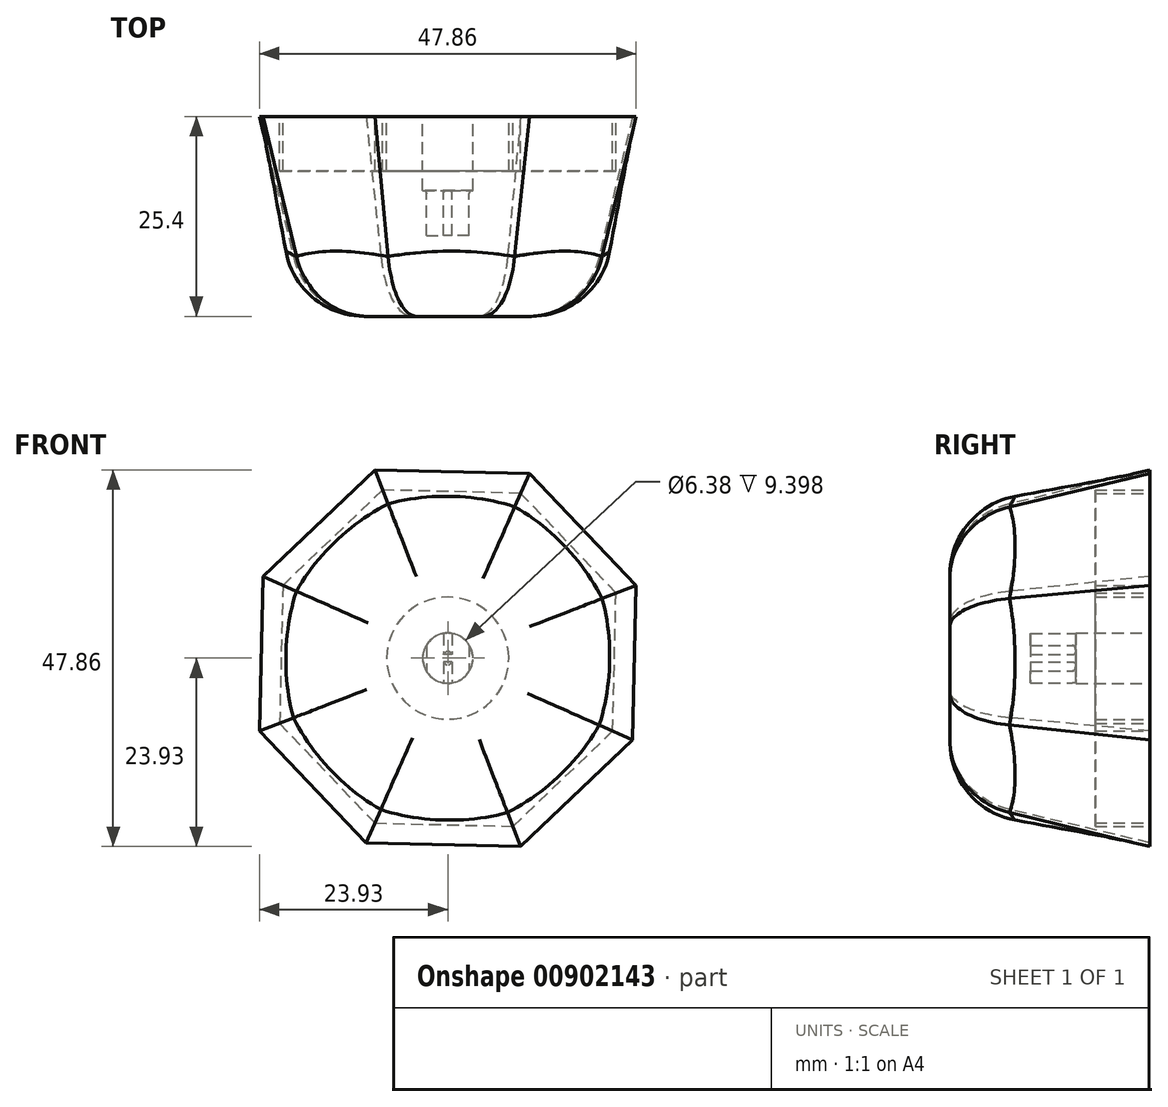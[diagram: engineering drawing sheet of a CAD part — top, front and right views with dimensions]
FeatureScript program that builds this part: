
annotation { "Feature Type Name" : "Feature", "Feature Type Description" : "" }
export const myFeature = defineFeature(function(context is Context, id is Id, definition is map)
    precondition{}
    {
        {
            var Q0;
            Q0=qCreatedBy(makeId("Front.planeOp"),FACE);
            var sketch = newSketch(context, id + "F0", { "sketchPlane" : qUnion([Q0])});
            skLineSegment(sketch, "E0.0", {"start": v(23.46, -10.38) * mm, "end": v(9.25, -23.93) * mm});
            skLineSegment(sketch, "E0.1", {"start": v(9.25, -23.93) * mm, "end": v(-10.38, -23.46) * mm});
            skLineSegment(sketch, "E0.2", {"start": v(-10.38, -23.46) * mm, "end": v(-23.93, -9.25) * mm});
            skLineSegment(sketch, "E0.3", {"start": v(-23.93, -9.25) * mm, "end": v(-23.46, 10.38) * mm});
            skLineSegment(sketch, "E0.4", {"start": v(-23.46, 10.38) * mm, "end": v(-9.25, 23.93) * mm});
            skLineSegment(sketch, "E0.5", {"start": v(-9.25, 23.93) * mm, "end": v(10.38, 23.46) * mm});
            skLineSegment(sketch, "E0.6", {"start": v(10.38, 23.46) * mm, "end": v(23.93, 9.25) * mm});
            skLineSegment(sketch, "E0.7", {"start": v(23.93, 9.25) * mm, "end": v(23.46, -10.38) * mm});
            skPoint(sketch, "E0.0.midPoint", {"position": v(16.36, -17.15) * mm});
            skSolve(sketch);
        }
        {
            var Q0;
            Q0=qCreatedBy(makeId("Front.planeOp"),FACE);
            cPlane(context, id + "F1", {"entities" : qUnion([Q0]), "cplaneType" : CPlaneType.OFFSET, "offset" : 25.4 * mm, "width" : 152.4 * mm, "height" : 152.4 * mm});
        }
        {
            var Q0;
            Q0=qCreatedBy(id+"F1.planeOp",FACE);
            var sketch = newSketch(context, id + "F2", { "sketchPlane" : qUnion([Q0])});
            skCircle(sketch, "E1", {"center": v(0, 0) * mm, "radius": 19.05 * mm});
            skSolve(sketch);
        }
        {
            var Q0;
            Q0=makeQuery(id+"F0.imprint","IMPRINT",FACE,{"disambiguationData":[TD([[makeQuery(id+"F0.imprint","IMPRINT",EDGE,{"derivedFrom":sQuery(id+"F0.wireOp",EDGE,"E0.0")}),-1.0]])]});
            var Q1;
            Q1=makeQuery(id+"F2.imprint","IMPRINT",FACE,{"disambiguationData":[TD([[makeQuery(id+"F2.imprint","IMPRINT",EDGE,{"derivedFrom":sQuery(id+"F2.wireOp",EDGE,"E1")}),1.0]])]});
            loft(context, id + "F3", {"sheetProfilesArray" : [{ "sheetProfileEntities" : qUnion([Q0]) }, { "sheetProfileEntities" : qUnion([Q1]) }]});
        }
        {
            var Q0;
            Q0=qCreatedBy(makeId("Front.planeOp"),FACE);
            var sketch = newSketch(context, id + "F4", { "sketchPlane" : qUnion([Q0])});
            skArc(sketch, "E2", {"start": v(2.72, 1.64) * mm, "mid": v(1.8, 2.62) * mm, "end": v(0.56, 3.13) * mm});
            skLineSegment(sketch, "E3.left", {"start": v(2.72, 1.64) * mm, "end": v(2.72, -1.64) * mm});
            skLineSegment(sketch, "E3.right", {"start": v(-2.72, 1.64) * mm, "end": v(-2.72, -1.64) * mm});
            skArc(sketch, "E4.trimOffspring", {"start": v(-2.72, -1.64) * mm, "mid": v(-1.8, -2.62) * mm, "end": v(-0.56, -3.13) * mm});
            skLineSegment(sketch, "E5.right", {"start": v(-0.56, 3.13) * mm, "end": v(-0.56, 0.48) * mm});
            skLineSegment(sketch, "E6.right", {"start": v(0.56, 3.13) * mm, "end": v(0.56, 0.48) * mm});
            skLineSegment(sketch, "E7.trimOffspring", {"start": v(0, -3.83) * mm, "end": v(0, -3.86) * mm});
            skPoint(sketch, "E5.left.start.orphan", {"position": v(0, 3.63) * mm});
            skLineSegment(sketch, "E8.top", {"start": v(0.56, 0.48) * mm, "end": v(-0.56, 0.48) * mm});
            skLineSegment(sketch, "E9.top", {"start": v(0.56, -0.48) * mm, "end": v(-0.56, -0.48) * mm});
            skLineSegment(sketch, "E10.trimOffspring", {"start": v(-0.56, -0.48) * mm, "end": v(-0.56, -3.13) * mm});
            skPoint(sketch, "E8.right.start.orphan", {"position": v(-0.56, 0) * mm});
            skLineSegment(sketch, "E11.trimOffspring", {"start": v(0.56, -0.48) * mm, "end": v(0.56, -3.13) * mm});
            skPoint(sketch, "E8.left.start.orphan", {"position": v(0.56, 0) * mm});
            skArc(sketch, "E12.trimOffspring", {"start": v(-0.56, 3.13) * mm, "mid": v(-1.8, 2.62) * mm, "end": v(-2.72, 1.64) * mm});
            skArc(sketch, "E13.trimOffspring", {"start": v(0.56, -3.13) * mm, "mid": v(1.8, -2.62) * mm, "end": v(2.72, -1.64) * mm});
            skSolve(sketch);
        }
        {
            var Q0;
            Q0=makeQuery(id+"F4.imprint","IMPRINT",FACE,{"disambiguationData":[TD([[makeQuery(id+"F4.imprint","IMPRINT",EDGE,{"derivedFrom":sQuery(id+"F4.wireOp",EDGE,"E2")}),1.0]])]});
            extrude(context, id + "F5", {"entities" : qUnion([Q0]), "operationType" : NewBodyOperationType.REMOVE, "depth" : 15.16 * mm, "offsetDistance" : 25.4 * mm});
        }
        {
            var Q0;
            Q0=qCreatedBy(makeId("Front.planeOp"),FACE);
            var sketch = newSketch(context, id + "F6", { "sketchPlane" : qUnion([Q0])});
            skCircle(sketch, "E14", {"center": v(0, 0) * mm, "radius": 3.2 * mm});
            skSolve(sketch);
        }
        {
            var Q0;
            Q0 = qSketchRegion(id + "F6", true);
            extrude(context, id + "F7", {"entities" : qUnion([Q0]), "operationType" : NewBodyOperationType.REMOVE, "depth" : 9.4 * mm, "offsetDistance" : 25.4 * mm});
        }
        {
            var Q0;
            Q0=makeQuery(id+"F7.boolean.opBoolean","INTERSECT",EDGE,{"derivedFrom":[makeQuery(id+"F5.boolean.opBoolean","COPY",FACE,{"derivedFrom":makeQuery(id+"F5.opExtrude","SWEPT_FACE",FACE,{"disambiguationData":[OSD([sQuery(id+"F4.wireOp",EDGE,"E3.left")])]})}),makeQuery(id+"F7.opExtrude","CAP_FACE",FACE,{"disambiguationData":[OSD([sQuery(id+"F6.wireOp",EDGE,"E14")])],"isStart":false})]});
            var Q1;
            Q1=makeQuery(id+"F7.boolean.opBoolean","INTERSECT",EDGE,{"derivedFrom":[makeQuery(id+"F5.boolean.opBoolean","COPY",FACE,{"derivedFrom":makeQuery(id+"F5.opExtrude","SWEPT_FACE",FACE,{"disambiguationData":[OSD([sQuery(id+"F4.wireOp",EDGE,"E3.right")])]})}),makeQuery(id+"F7.opExtrude","CAP_FACE",FACE,{"disambiguationData":[OSD([sQuery(id+"F6.wireOp",EDGE,"E14")])],"isStart":false})]});
            var Q2;
            Q2=makeQuery(id+"F7.boolean.opBoolean","INTERSECT",EDGE,{"derivedFrom":[makeQuery(id+"F5.boolean.opBoolean","COPY",FACE,{"derivedFrom":makeQuery(id+"F5.opExtrude","SWEPT_FACE",FACE,{"disambiguationData":[OSD([sQuery(id+"F4.wireOp",EDGE,"E5.right")])]})}),makeQuery(id+"F7.opExtrude","CAP_FACE",FACE,{"disambiguationData":[OSD([sQuery(id+"F6.wireOp",EDGE,"E14")])],"isStart":false})]});
            var Q3;
            Q3=makeQuery(id+"F7.boolean.opBoolean","INTERSECT",EDGE,{"derivedFrom":[makeQuery(id+"F5.boolean.opBoolean","COPY",FACE,{"derivedFrom":makeQuery(id+"F5.opExtrude","SWEPT_FACE",FACE,{"disambiguationData":[OSD([sQuery(id+"F4.wireOp",EDGE,"E6.right")])]})}),makeQuery(id+"F7.opExtrude","CAP_FACE",FACE,{"disambiguationData":[OSD([sQuery(id+"F6.wireOp",EDGE,"E14")])],"isStart":false})]});
            var Q4;
            Q4=makeQuery(id+"F7.boolean.opBoolean","INTERSECT",EDGE,{"derivedFrom":[makeQuery(id+"F5.boolean.opBoolean","COPY",FACE,{"derivedFrom":makeQuery(id+"F5.opExtrude","SWEPT_FACE",FACE,{"disambiguationData":[OSD([sQuery(id+"F4.wireOp",EDGE,"E8.top")])]})}),makeQuery(id+"F7.opExtrude","CAP_FACE",FACE,{"disambiguationData":[OSD([sQuery(id+"F6.wireOp",EDGE,"E14")])],"isStart":false})]});
            var Q5;
            Q5=makeQuery(id+"F7.boolean.opBoolean","INTERSECT",EDGE,{"derivedFrom":[makeQuery(id+"F5.boolean.opBoolean","COPY",FACE,{"derivedFrom":makeQuery(id+"F5.opExtrude","SWEPT_FACE",FACE,{"disambiguationData":[OSD([sQuery(id+"F4.wireOp",EDGE,"E11.trimOffspring")])]})}),makeQuery(id+"F7.opExtrude","CAP_FACE",FACE,{"disambiguationData":[OSD([sQuery(id+"F6.wireOp",EDGE,"E14")])],"isStart":false})]});
            var Q6;
            Q6=makeQuery(id+"F7.boolean.opBoolean","INTERSECT",EDGE,{"derivedFrom":[makeQuery(id+"F5.boolean.opBoolean","COPY",FACE,{"derivedFrom":makeQuery(id+"F5.opExtrude","SWEPT_FACE",FACE,{"disambiguationData":[OSD([sQuery(id+"F4.wireOp",EDGE,"E9.top")])]})}),makeQuery(id+"F7.opExtrude","CAP_FACE",FACE,{"disambiguationData":[OSD([sQuery(id+"F6.wireOp",EDGE,"E14")])],"isStart":false})]});
            var Q7;
            Q7=makeQuery(id+"F7.boolean.opBoolean","INTERSECT",EDGE,{"derivedFrom":[makeQuery(id+"F5.boolean.opBoolean","COPY",FACE,{"derivedFrom":makeQuery(id+"F5.opExtrude","SWEPT_FACE",FACE,{"disambiguationData":[OSD([sQuery(id+"F4.wireOp",EDGE,"E10.trimOffspring")])]})}),makeQuery(id+"F7.opExtrude","CAP_FACE",FACE,{"disambiguationData":[OSD([sQuery(id+"F6.wireOp",EDGE,"E14")])],"isStart":false})]});
            fillet(context, id + "F8", {"entities" : qUnion([Q0, Q1, Q2, Q3, Q4, Q5, Q6, Q7]), "radius" : 0.44 * mm, "tangentPropagation" : true, "allowEdgeOverflow" : false});
        }
        {
            var Q0;
            Q0=makeQuery(id+"F3.opLoft","MID_CAP_EDGE",EDGE,{"disambiguationData":[OSD([sQuery(id+"F0.wireOp",EDGE,"E0.0"),sQuery(id+"F0.wireOp",EDGE,"E0.6"),sQuery(id+"F0.wireOp",EDGE,"E0.7"),sQuery(id+"F2.wireOp",EDGE,"E1")])],"capPos":1.0});
            var Q1;
            Q1=makeQuery(id+"F3.opLoft","MID_CAP_EDGE",EDGE,{"disambiguationData":[OSD([sQuery(id+"F0.wireOp",EDGE,"E0.5"),sQuery(id+"F0.wireOp",EDGE,"E0.6"),sQuery(id+"F0.wireOp",EDGE,"E0.7"),sQuery(id+"F2.wireOp",EDGE,"E1")])],"capPos":1.0});
            var Q2;
            Q2=makeQuery(id+"F3.opLoft","MID_CAP_EDGE",EDGE,{"disambiguationData":[OSD([sQuery(id+"F0.wireOp",EDGE,"E0.4"),sQuery(id+"F0.wireOp",EDGE,"E0.5"),sQuery(id+"F0.wireOp",EDGE,"E0.6"),sQuery(id+"F2.wireOp",EDGE,"E1")])],"capPos":1.0});
            var Q3;
            Q3=makeQuery(id+"F3.opLoft","MID_CAP_EDGE",EDGE,{"disambiguationData":[OSD([sQuery(id+"F0.wireOp",EDGE,"E0.3"),sQuery(id+"F0.wireOp",EDGE,"E0.4"),sQuery(id+"F0.wireOp",EDGE,"E0.5"),sQuery(id+"F2.wireOp",EDGE,"E1")])],"capPos":1.0});
            var Q4;
            Q4=makeQuery(id+"F3.opLoft","MID_CAP_EDGE",EDGE,{"disambiguationData":[OSD([sQuery(id+"F0.wireOp",EDGE,"E0.2"),sQuery(id+"F0.wireOp",EDGE,"E0.3"),sQuery(id+"F0.wireOp",EDGE,"E0.4"),sQuery(id+"F2.wireOp",EDGE,"E1")])],"capPos":1.0});
            var Q5;
            Q5=makeQuery(id+"F3.opLoft","MID_CAP_EDGE",EDGE,{"disambiguationData":[OSD([sQuery(id+"F0.wireOp",EDGE,"E0.1"),sQuery(id+"F0.wireOp",EDGE,"E0.2"),sQuery(id+"F0.wireOp",EDGE,"E0.3"),sQuery(id+"F2.wireOp",EDGE,"E1")])],"capPos":1.0});
            var Q6;
            Q6=makeQuery(id+"F3.opLoft","MID_CAP_EDGE",EDGE,{"disambiguationData":[OSD([sQuery(id+"F0.wireOp",EDGE,"E0.0"),sQuery(id+"F0.wireOp",EDGE,"E0.1"),sQuery(id+"F0.wireOp",EDGE,"E0.2"),sQuery(id+"F0.wireOp",EDGE,"E0.7"),sQuery(id+"F2.wireOp",EDGE,"E1")])],"capPos":1.0});
            var Q7;
            Q7=makeQuery(id+"F3.opLoft","MID_CAP_EDGE",EDGE,{"disambiguationData":[OSD([sQuery(id+"F0.wireOp",EDGE,"E0.0"),sQuery(id+"F0.wireOp",EDGE,"E0.7"),sQuery(id+"F2.wireOp",EDGE,"E1")])],"capPos":1.0});
            fillet(context, id + "F9", {"entities" : qUnion([Q0, Q1, Q2, Q3, Q4, Q5, Q6, Q7]), "radius" : 10.1 * mm, "tangentPropagation" : true, "allowEdgeOverflow" : false});
        }
        {
            var Q0;
            Q0=qCreatedBy(makeId("Front.planeOp"),FACE);
            var sketch = newSketch(context, id + "F10", { "sketchPlane" : qUnion([Q0])});
            skLineSegment(sketch, "E15.0", {"start": v(20.95, -9.27) * mm, "end": v(21.36, 8.26) * mm});
            skLineSegment(sketch, "E15.1", {"start": v(8.26, -21.36) * mm, "end": v(20.95, -9.27) * mm});
            skLineSegment(sketch, "E15.2", {"start": v(21.36, 8.26) * mm, "end": v(9.27, 20.95) * mm});
            skLineSegment(sketch, "E15.3", {"start": v(-9.27, -20.95) * mm, "end": v(8.26, -21.36) * mm});
            skLineSegment(sketch, "E15.4", {"start": v(9.27, 20.95) * mm, "end": v(-8.26, 21.36) * mm});
            skLineSegment(sketch, "E15.5", {"start": v(-8.26, 21.36) * mm, "end": v(-20.95, 9.27) * mm});
            skLineSegment(sketch, "E15.6", {"start": v(-20.95, 9.27) * mm, "end": v(-21.36, -8.26) * mm});
            skLineSegment(sketch, "E15.7", {"start": v(-21.36, -8.26) * mm, "end": v(-9.27, -20.95) * mm});
            skCircle(sketch, "E16", {"center": v(0, 0) * mm, "radius": 7.76 * mm});
            skSolve(sketch);
        }
        {
            var Q0;
            Q0=makeQuery(id+"F10.imprint","IMPRINT",FACE,{"disambiguationData":[TD([[makeQuery(id+"F10.imprint","IMPRINT",EDGE,{"derivedFrom":sQuery(id+"F10.wireOp",EDGE,"E15.0")}),1.0]])]});
            extrude(context, id + "F11", {"entities" : qUnion([Q0]), "operationType" : NewBodyOperationType.REMOVE, "depth" : 6.96 * mm, "offsetDistance" : 25.4 * mm});
        }
    });
